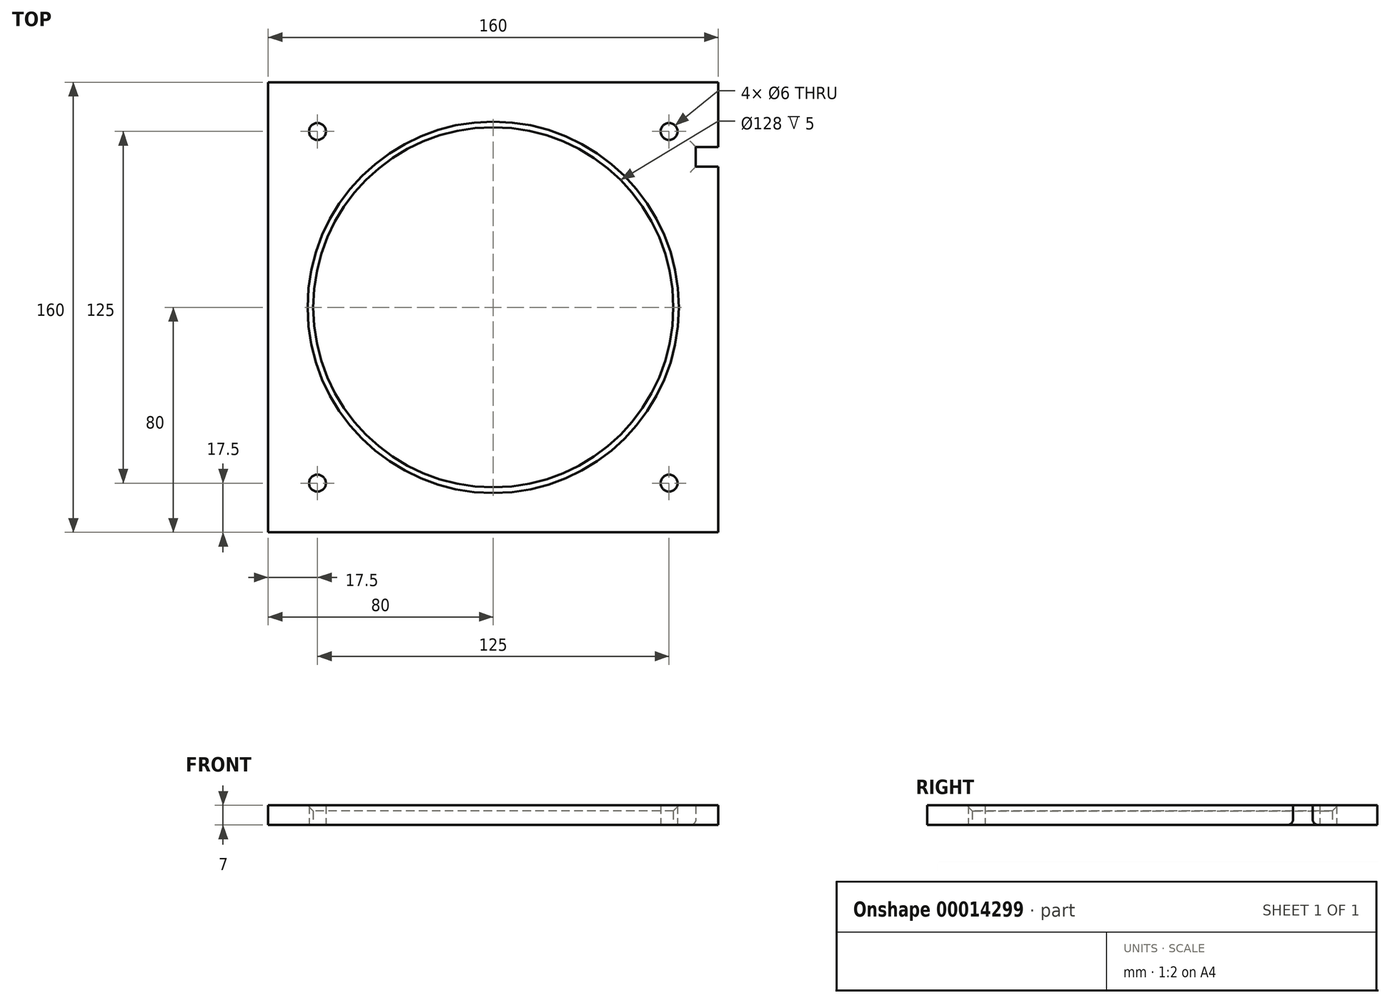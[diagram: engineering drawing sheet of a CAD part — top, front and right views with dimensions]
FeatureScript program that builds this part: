
annotation { "Feature Type Name" : "Feature", "Feature Type Description" : "" }
export const myFeature = defineFeature(function(context is Context, id is Id, definition is map)
    precondition{}
    {
        {
            var Q0;
            Q0=qCreatedBy(makeId("Top.planeOp"),FACE);
            var sketch = newSketch(context, id + "F0", { "sketchPlane" : qUnion([Q0])});
            skLineSegment(sketch, "E0.bottom", {"start": v(-80, 80) * mm, "end": v(80, 80) * mm});
            skLineSegment(sketch, "E0.top", {"start": v(-80, -80) * mm, "end": v(80, -80) * mm});
            skLineSegment(sketch, "E0.left", {"start": v(-80, 80) * mm, "end": v(-80, -80) * mm});
            skLineSegment(sketch, "E0.right", {"start": v(80, 80) * mm, "end": v(80, -80) * mm});
            skLineSegment(sketch, "E1", {"start": v(0, 0) * mm, "end": v(-80, 0) * mm, "construction": true});
            skLineSegment(sketch, "E2", {"start": v(0, 0) * mm, "end": v(0, 80) * mm, "construction": true});
            skCircle(sketch, "E3", {"center": v(0, 0) * mm, "radius": 64 * mm});
            skLineSegment(sketch, "E4", {"start": v(-62.5, 62.5) * mm, "end": v(62.5, 62.5) * mm, "construction": true});
            skLineSegment(sketch, "E5", {"start": v(62.5, 62.5) * mm, "end": v(62.5, -62.5) * mm, "construction": true});
            skLineSegment(sketch, "E6", {"start": v(62.5, -62.5) * mm, "end": v(-62.5, -62.5) * mm, "construction": true});
            skLineSegment(sketch, "E7", {"start": v(-62.5, -62.5) * mm, "end": v(-62.5, 62.5) * mm, "construction": true});
            skLineSegment(sketch, "E8", {"start": v(-62.5, 62.5) * mm, "end": v(-80, 62.5) * mm, "construction": true});
            skLineSegment(sketch, "E9", {"start": v(-62.5, 62.5) * mm, "end": v(-62.5, 80) * mm, "construction": true});
            skCircle(sketch, "E10", {"center": v(-62.5, 62.5) * mm, "radius": 3 * mm});
            skCircle(sketch, "E11", {"center": v(-62.5, -62.5) * mm, "radius": 3 * mm});
            skCircle(sketch, "E12", {"center": v(62.5, -62.5) * mm, "radius": 3 * mm});
            skCircle(sketch, "E13", {"center": v(62.5, 62.5) * mm, "radius": 3 * mm});
            skLineSegment(sketch, "E14", {"start": v(80, 57) * mm, "end": v(72, 57) * mm});
            skLineSegment(sketch, "E15", {"start": v(72, 57) * mm, "end": v(72, 50) * mm});
            skLineSegment(sketch, "E16", {"start": v(72, 50) * mm, "end": v(80, 50) * mm});
            skSolve(sketch);
        }
        {
            var Q0;
            Q0=makeQuery(id+"F0.imprint","IMPRINT",FACE,{"disambiguationData":[TD([[makeQuery(id+"F0.imprint","IMPRINT",EDGE,{"derivedFrom":sQuery(id+"F0.wireOp",EDGE,"E0.bottom")}),-1.0]])]});
            extrude(context, id + "F1", {"entities" : qUnion([Q0]), "depth" : 7 * mm});
        }
        {
            var Q0;
            Q0=makeQuery(id+"F1.opExtrude","CAP_EDGE",EDGE,{"disambiguationData":[OSD([sQuery(id+"F0.wireOp",EDGE,"E3")])],"isStart":false});
            chamfer(context, id + "F2", {"entities" : qUnion([Q0]), "width" : 2 * mm, "tangentPropagation" : true});
        }
        {
            var Q0;
            Q0=makeQuery(id+"F1.opExtrude","CAP_EDGE",EDGE,{"disambiguationData":[OSD([sQuery(id+"F0.wireOp",EDGE,"E14")])],"isStart":true});
            var Q1;
            Q1=makeQuery(id+"F1.opExtrude","CAP_EDGE",EDGE,{"disambiguationData":[OSD([sQuery(id+"F0.wireOp",EDGE,"E15")])],"isStart":true});
            var Q2;
            Q2=makeQuery(id+"F1.opExtrude","CAP_EDGE",EDGE,{"disambiguationData":[OSD([sQuery(id+"F0.wireOp",EDGE,"E16")])],"isStart":true});
            fillet(context, id + "F3", {"entities" : qUnion([Q0, Q1, Q2]), "radius" : 2 * mm, "tangentPropagation" : true, "allowEdgeOverflow" : false});
        }
    });
